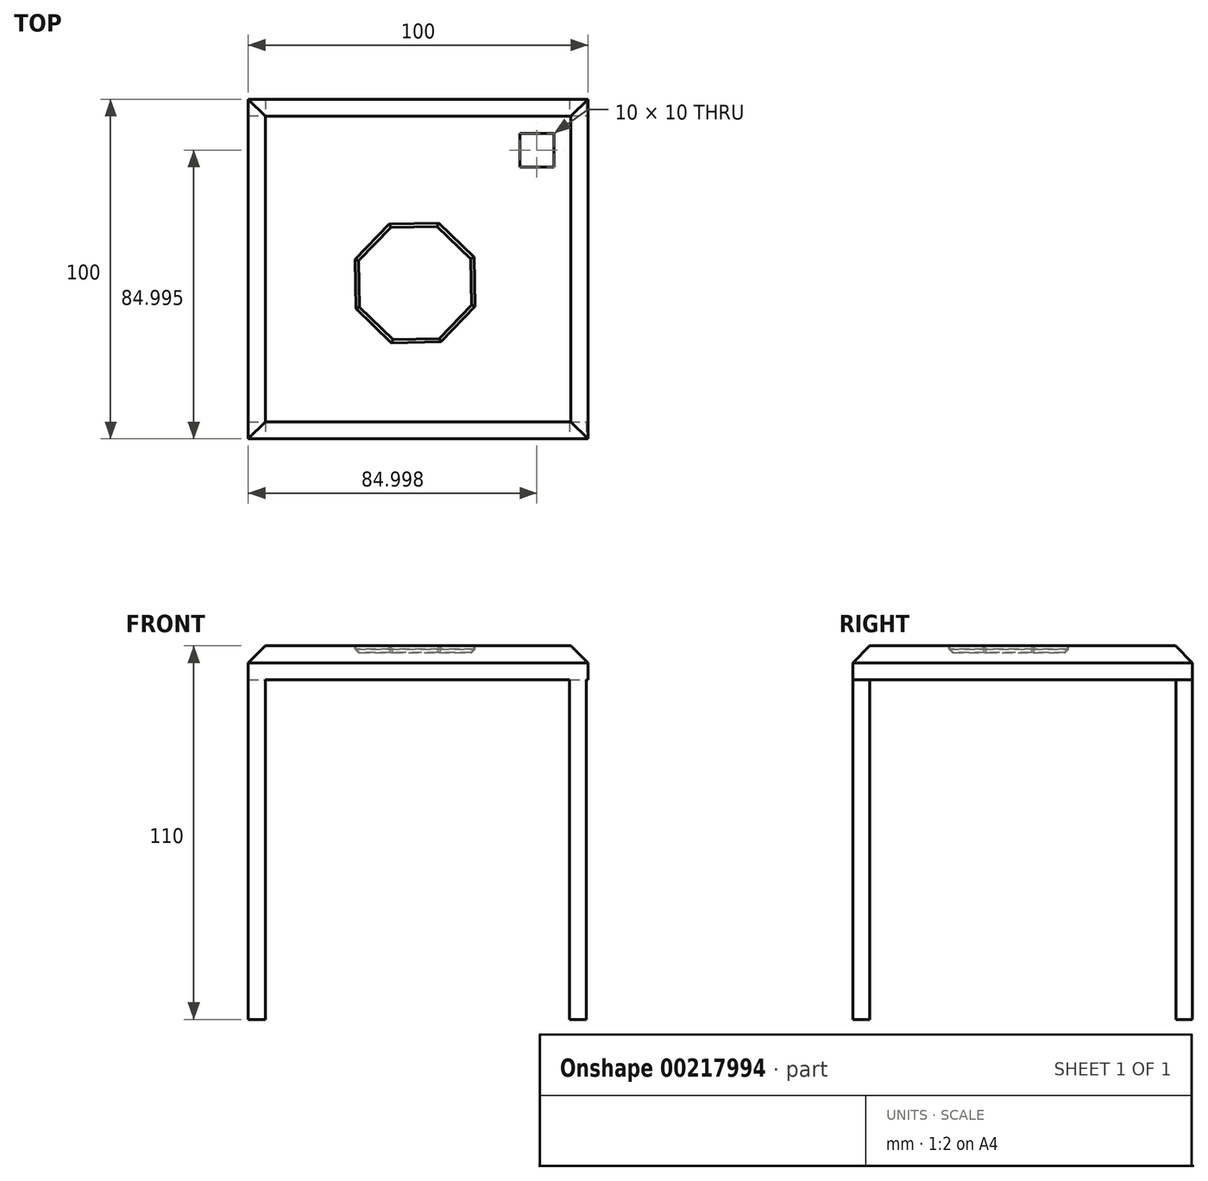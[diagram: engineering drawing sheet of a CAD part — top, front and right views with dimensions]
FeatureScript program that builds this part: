
annotation { "Feature Type Name" : "Feature", "Feature Type Description" : "" }
export const myFeature = defineFeature(function(context is Context, id is Id, definition is map)
    precondition{}
    {
        {
            var Q0;
            Q0=qCreatedBy(makeId("Top.planeOp"),FACE);
            var sketch = newSketch(context, id + "F0", { "sketchPlane" : qUnion([Q0])});
            skLineSegment(sketch, "E0.bottom", {"start": v(-49.13, 54.1) * mm, "end": v(50.87, 54.1) * mm});
            skLineSegment(sketch, "E0.top", {"start": v(-49.13, -45.9) * mm, "end": v(50.87, -45.9) * mm});
            skLineSegment(sketch, "E0.left", {"start": v(-49.13, 54.1) * mm, "end": v(-49.13, -45.9) * mm});
            skLineSegment(sketch, "E0.right", {"start": v(50.87, 54.1) * mm, "end": v(50.87, -45.9) * mm});
            skSolve(sketch);
        }
        {
            var Q0;
            Q0=makeQuery(id+"F0.imprint","IMPRINT",FACE,{"disambiguationData":[TD([[makeQuery(id+"F0.imprint","IMPRINT",EDGE,{"derivedFrom":sQuery(id+"F0.wireOp",EDGE,"E0.bottom")}),-1.0]])]});
            var sketch = newSketch(context, id + "F1", { "sketchPlane" : qUnion([Q0])});
            skCircle(sketch, "E1.cCircle", {"center": v(0, 0) * mm, "radius": 17.5 * mm, "construction": true});
            skLineSegment(sketch, "E1.0", {"start": v(-17.63, 6.92) * mm, "end": v(-7.57, 17.36) * mm});
            skLineSegment(sketch, "E1.1", {"start": v(-7.57, 17.36) * mm, "end": v(6.92, 17.63) * mm});
            skLineSegment(sketch, "E1.2", {"start": v(6.92, 17.63) * mm, "end": v(17.36, 7.57) * mm});
            skLineSegment(sketch, "E1.3", {"start": v(17.36, 7.57) * mm, "end": v(17.63, -6.92) * mm});
            skLineSegment(sketch, "E1.4", {"start": v(17.63, -6.92) * mm, "end": v(7.57, -17.36) * mm});
            skLineSegment(sketch, "E1.5", {"start": v(7.57, -17.36) * mm, "end": v(-6.92, -17.63) * mm});
            skLineSegment(sketch, "E1.6", {"start": v(-6.92, -17.63) * mm, "end": v(-17.36, -7.57) * mm});
            skLineSegment(sketch, "E1.7", {"start": v(-17.36, -7.57) * mm, "end": v(-17.63, 6.92) * mm});
            skPoint(sketch, "E1.0.midPoint", {"position": v(-12.6, 12.14) * mm});
            skSolve(sketch);
        }
        {
            var Q0;
            Q0 = qSketchRegion(id + "F0", true);
            extrude(context, id + "F2", {"entities" : qUnion([Q0]), "oppositeDirection" : true, "depth" : 10 * mm});
        }
        {
            var Q0;
            Q0=makeQuery(id+"F1.imprint","IMPRINT",FACE,{"disambiguationData":[TD([[makeQuery(id+"F1.imprint","IMPRINT",EDGE,{"derivedFrom":sQuery(id+"F1.wireOp",EDGE,"E1.0")}),1.0]])]});
            var sketch = newSketch(context, id + "F3", { "sketchPlane" : qUnion([Q0])});
            skLineSegment(sketch, "E2.bottom", {"start": v(30.87, 44.1) * mm, "end": v(40.87, 44.1) * mm});
            skLineSegment(sketch, "E2.top", {"start": v(30.87, 34.1) * mm, "end": v(40.87, 34.1) * mm});
            skLineSegment(sketch, "E2.left", {"start": v(30.87, 44.1) * mm, "end": v(30.87, 34.1) * mm});
            skLineSegment(sketch, "E2.right", {"start": v(40.87, 44.1) * mm, "end": v(40.87, 34.1) * mm});
            skSolve(sketch);
        }
        {
            var Q0;
            Q0=makeQuery(id+"F2.opExtrude","CAP_EDGE",EDGE,{"disambiguationData":[OSD([sQuery(id+"F0.wireOp",EDGE,"E0.top")])],"isStart":true});
            var Q1;
            Q1=makeQuery(id+"F2.opExtrude","CAP_EDGE",EDGE,{"disambiguationData":[OSD([sQuery(id+"F0.wireOp",EDGE,"E0.left")])],"isStart":true});
            var Q2;
            Q2=makeQuery(id+"F2.opExtrude","CAP_EDGE",EDGE,{"disambiguationData":[OSD([sQuery(id+"F0.wireOp",EDGE,"E0.bottom")])],"isStart":true});
            var Q3;
            Q3=makeQuery(id+"F2.opExtrude","CAP_EDGE",EDGE,{"disambiguationData":[OSD([sQuery(id+"F0.wireOp",EDGE,"E0.right")])],"isStart":true});
            chamfer(context, id + "F4", {"entities" : qUnion([Q0, Q1, Q2, Q3]), "chamferType" : ChamferType.TWO_OFFSETS, "width1" : 5 * mm, "oppositeDirection" : false, "width2" : 5 * mm, "tangentPropagation" : true});
        }
        {
            var Q0;
            Q0=makeQuery(id+"F3.imprint","IMPRINT",FACE,{"disambiguationData":[TD([[makeQuery(id+"F3.imprint","IMPRINT",EDGE,{"derivedFrom":sQuery(id+"F3.wireOp",EDGE,"E2.bottom")}),-1.0]])]});
            extrude(context, id + "F5", {"entities" : qUnion([Q0]), "operationType" : NewBodyOperationType.REMOVE, "oppositeDirection" : true, "depth" : 34 * mm});
        }
        {
            var Q0;
            Q0=makeQuery(id+"F1.imprint","IMPRINT",FACE,{"disambiguationData":[TD([[makeQuery(id+"F1.imprint","IMPRINT",EDGE,{"derivedFrom":sQuery(id+"F1.wireOp",EDGE,"E1.0")}),-1.0]])]});
            extrude(context, id + "F6", {"entities" : qUnion([Q0]), "operationType" : NewBodyOperationType.REMOVE, "oppositeDirection" : true, "depth" : 2 * mm});
        }
        {
            var Q0;
            Q0=makeQuery(id+"F6.boolean.opBoolean","COPY",FACE,{"derivedFrom":makeQuery(id+"F6.opExtrude","CAP_FACE",FACE,{"disambiguationData":[OSD([sQuery(id+"F1.wireOp",EDGE,"E1.0"),sQuery(id+"F1.wireOp",EDGE,"E1.1"),sQuery(id+"F1.wireOp",EDGE,"E1.2"),sQuery(id+"F1.wireOp",EDGE,"E1.3"),sQuery(id+"F1.wireOp",EDGE,"E1.4"),sQuery(id+"F1.wireOp",EDGE,"E1.5"),sQuery(id+"F1.wireOp",EDGE,"E1.6"),sQuery(id+"F1.wireOp",EDGE,"E1.7")])],"isStart":false})});
            chamfer(context, id + "F7", {"entities" : qUnion([Q0]), "width" : 1 * mm, "tangentPropagation" : true});
        }
        {
            var Q0;
            Q0=makeQuery(id+"F2.opExtrude","CAP_FACE",FACE,{"disambiguationData":[OSD([sQuery(id+"F0.wireOp",EDGE,"E0.bottom"),sQuery(id+"F0.wireOp",EDGE,"E0.top"),sQuery(id+"F0.wireOp",EDGE,"E0.left"),sQuery(id+"F0.wireOp",EDGE,"E0.right")])],"isStart":false});
            var sketch = newSketch(context, id + "F8", { "sketchPlane" : qUnion([Q0])});
            skLineSegment(sketch, "E3.bottom", {"start": v(-49.13, 40.9) * mm, "end": v(-44.13, 40.9) * mm});
            skLineSegment(sketch, "E3.top", {"start": v(-49.13, 45.9) * mm, "end": v(-44.13, 45.9) * mm});
            skLineSegment(sketch, "E3.left", {"start": v(-49.13, 40.9) * mm, "end": v(-49.13, 45.9) * mm});
            skLineSegment(sketch, "E3.right", {"start": v(-44.13, 40.9) * mm, "end": v(-44.13, 45.9) * mm});
            skLineSegment(sketch, "E4.0.1.0", {"start": v(-49.13, -54.2) * mm, "end": v(-49.13, -49.2) * mm});
            skLineSegment(sketch, "E4.0.1.1", {"start": v(-49.13, -54.2) * mm, "end": v(-44.13, -54.2) * mm});
            skLineSegment(sketch, "E4.0.1.2", {"start": v(-44.13, -54.2) * mm, "end": v(-44.13, -49.2) * mm});
            skLineSegment(sketch, "E4.0.1.3", {"start": v(-49.13, -49.2) * mm, "end": v(-44.13, -49.2) * mm});
            skLineSegment(sketch, "E4.1.0.0", {"start": v(-1.83, 40.9) * mm, "end": v(-1.83, 45.9) * mm});
            skLineSegment(sketch, "E4.1.0.1", {"start": v(-1.83, 40.9) * mm, "end": v(3.17, 40.9) * mm});
            skLineSegment(sketch, "E4.1.0.2", {"start": v(3.17, 40.9) * mm, "end": v(3.17, 45.9) * mm});
            skLineSegment(sketch, "E4.1.0.3", {"start": v(-1.83, 45.9) * mm, "end": v(3.17, 45.9) * mm});
            skLineSegment(sketch, "E4.1.1.0", {"start": v(-1.83, -54.2) * mm, "end": v(-1.83, -49.2) * mm});
            skLineSegment(sketch, "E4.1.1.1", {"start": v(-1.83, -54.2) * mm, "end": v(3.17, -54.2) * mm});
            skLineSegment(sketch, "E4.1.1.2", {"start": v(3.17, -54.2) * mm, "end": v(3.17, -49.2) * mm});
            skLineSegment(sketch, "E4.1.1.3", {"start": v(-1.83, -49.2) * mm, "end": v(3.17, -49.2) * mm});
            skLineSegment(sketch, "E4.2.0.0", {"start": v(45.47, 40.9) * mm, "end": v(45.47, 45.9) * mm});
            skLineSegment(sketch, "E4.2.0.1", {"start": v(45.47, 40.9) * mm, "end": v(50.47, 40.9) * mm});
            skLineSegment(sketch, "E4.2.0.2", {"start": v(50.47, 40.9) * mm, "end": v(50.47, 45.9) * mm});
            skLineSegment(sketch, "E4.2.0.3", {"start": v(45.47, 45.9) * mm, "end": v(50.47, 45.9) * mm});
            skLineSegment(sketch, "E4.2.1.0", {"start": v(45.47, -54.2) * mm, "end": v(45.47, -49.2) * mm});
            skLineSegment(sketch, "E4.2.1.1", {"start": v(45.47, -54.2) * mm, "end": v(50.47, -54.2) * mm});
            skLineSegment(sketch, "E4.2.1.2", {"start": v(50.47, -54.2) * mm, "end": v(50.47, -49.2) * mm});
            skLineSegment(sketch, "E4.2.1.3", {"start": v(45.47, -49.2) * mm, "end": v(50.47, -49.2) * mm});
            skLineSegment(sketch, "E4.direction1", {"start": v(-49.13, 40.9) * mm, "end": v(-1.83, 40.9) * mm, "construction": true});
            skLineSegment(sketch, "E4.direction2", {"start": v(-49.13, 40.9) * mm, "end": v(-49.13, -54.2) * mm, "construction": true});
            skSolve(sketch);
        }
        {
            var Q0;
            {var subQ3=sQuery(id+"F8.wireOp",EDGE,"E4.0.1.3");Q0=makeQuery(id+"F8.imprint","IMPRINT",FACE,{"disambiguationData":[TD([[makeQuery(id+"F8.imprint","IMPRINT",EDGE,{"derivedFrom":subQ3}),-1.0]])]});}
            var Q1;
            Q1=makeQuery(id+"F8.imprint","IMPRINT",FACE,{"disambiguationData":[TD([[makeQuery(id+"F8.imprint","IMPRINT",EDGE,{"derivedFrom":sQuery(id+"F8.wireOp",EDGE,"E3.bottom")}),1.0]])]});
            var Q2;
            {var subQ0=sQuery(id+"F8.wireOp",EDGE,"E4.2.1.3");Q2=makeQuery(id+"F8.imprint","IMPRINT",FACE,{"disambiguationData":[TD([[makeQuery(id+"F8.imprint","IMPRINT",EDGE,{"derivedFrom":subQ0}),-1.0]])]});}
            var Q3;
            Q3=makeQuery(id+"F8.imprint","IMPRINT",FACE,{"disambiguationData":[TD([[makeQuery(id+"F8.imprint","IMPRINT",EDGE,{"derivedFrom":sQuery(id+"F8.wireOp",EDGE,"E4.2.0.0")}),-1.0]])]});
            extrude(context, id + "F9", {"entities" : qUnion([Q0, Q1, Q2, Q3]), "operationType" : NewBodyOperationType.ADD, "depth" : 100 * mm});
        }
    });
